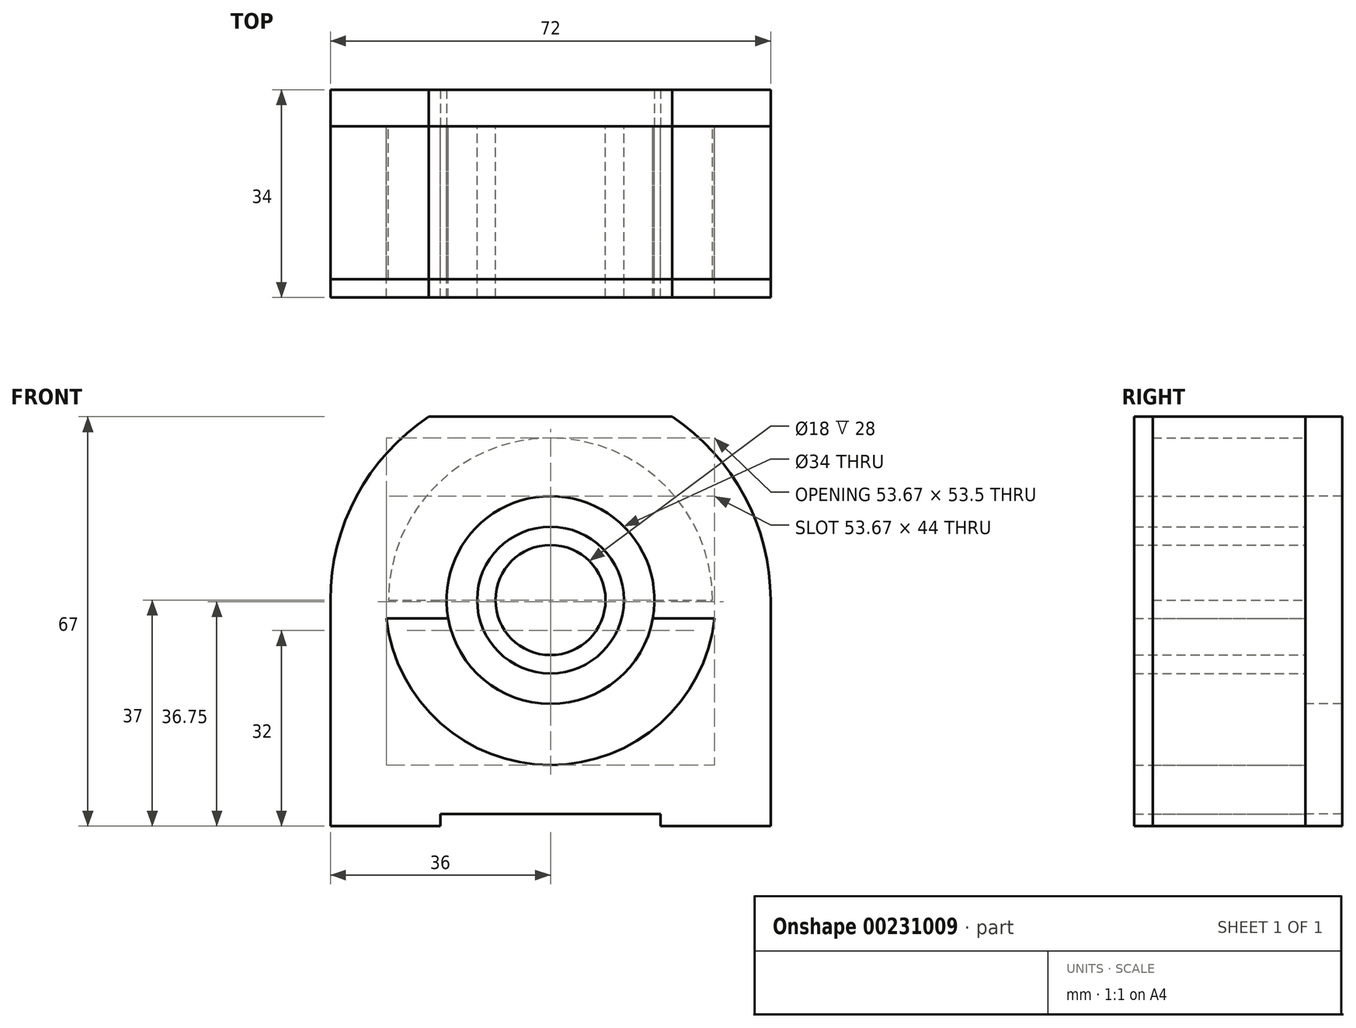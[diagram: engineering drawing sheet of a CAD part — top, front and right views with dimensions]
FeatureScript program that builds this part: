
annotation { "Feature Type Name" : "Feature", "Feature Type Description" : "" }
export const myFeature = defineFeature(function(context is Context, id is Id, definition is map)
    precondition{}
    {
        {
            var Q0;
            Q0=qCreatedBy(makeId("Front.planeOp"),FACE);
            var sketch = newSketch(context, id + "F0", { "sketchPlane" : qUnion([Q0])});
            skLineSegment(sketch, "E0", {"start": v(0, 0) * mm, "end": v(18, 0) * mm});
            skLineSegment(sketch, "E1", {"start": v(72, 0) * mm, "end": v(72, 37) * mm});
            skLineSegment(sketch, "E2", {"start": v(55.9, 67) * mm, "end": v(16.1, 67) * mm});
            skLineSegment(sketch, "E3", {"start": v(0, 37) * mm, "end": v(0, 0) * mm});
            skLineSegment(sketch, "E4", {"start": v(72, 37) * mm, "end": v(-6.12, 37) * mm, "construction": true});
            skLineSegment(sketch, "E5", {"start": v(36, 2) * mm, "end": v(36, 89.75) * mm, "construction": true});
            skPoint(sketch, "E5.endSnap0", {"position": v(36, 67) * mm});
            skLineSegment(sketch, "E6", {"start": v(36, 2) * mm, "end": v(36, 37) * mm, "construction": true});
            skArc(sketch, "E7", {"start": v(16.1, 67) * mm, "mid": v(4.28, 54.02) * mm, "end": v(0, 37) * mm});
            skArc(sketch, "E8", {"start": v(9.17, 34) * mm, "mid": v(36, 10) * mm, "end": v(62.83, 34) * mm});
            skArc(sketch, "E9", {"start": v(62.5, 37) * mm, "mid": v(36, 63.5) * mm, "end": v(9.5, 37) * mm});
            skCircle(sketch, "E10", {"center": v(36, 37) * mm, "radius": 12 * mm});
            skCircle(sketch, "E11", {"center": v(36, 37) * mm, "radius": 9 * mm});
            skPoint(sketch, "E12.orphan", {"position": v(0, 67) * mm});
            skPoint(sketch, "E13.orphan", {"position": v(72, 67) * mm});
            skLineSegment(sketch, "E14.top", {"start": v(18, 2) * mm, "end": v(54, 2) * mm});
            skLineSegment(sketch, "E14.left", {"start": v(18, 0) * mm, "end": v(18, 2) * mm});
            skLineSegment(sketch, "E14.right", {"start": v(54, 0) * mm, "end": v(54, 2) * mm});
            skLineSegment(sketch, "E15.trimOffspring", {"start": v(54, 0) * mm, "end": v(72, 0) * mm});
            skPoint(sketch, "E16.end.orphan", {"position": v(54, 0) * mm});
            skArc(sketch, "E17.trimOffspring", {"start": v(72, 37) * mm, "mid": v(67.72, 54.02) * mm, "end": v(55.9, 67) * mm});
            skPoint(sketch, "E18.orphan", {"position": v(36, 0) * mm});
            skLineSegment(sketch, "E19", {"start": v(0, 0) * mm, "end": v(0, 34) * mm});
            skLineSegment(sketch, "E20", {"start": v(0, 34) * mm, "end": v(72, 34) * mm, "construction": true});
            skLineSegment(sketch, "E21", {"start": v(0, 34) * mm, "end": v(19.27, 34) * mm});
            skLineSegment(sketch, "E22", {"start": v(52.73, 34) * mm, "end": v(72, 34) * mm});
            skLineSegment(sketch, "E23", {"start": v(72, 34) * mm, "end": v(62.83, 34) * mm});
            skLineSegment(sketch, "E24", {"start": v(0, 34) * mm, "end": v(9.17, 34) * mm});
            skLineSegment(sketch, "E25", {"start": v(9.17, 34) * mm, "end": v(9.67, 34) * mm});
            skLineSegment(sketch, "E26", {"start": v(9.67, 34) * mm, "end": v(16.23, 34) * mm});
            skArc(sketch, "E27.trimOffspring", {"start": v(19.27, 34) * mm, "mid": v(36, 20) * mm, "end": v(52.73, 34) * mm});
            skLineSegment(sketch, "E28", {"start": v(9.5, 37) * mm, "end": v(24, 37) * mm});
            skLineSegment(sketch, "E29", {"start": v(48, 37) * mm, "end": v(62.5, 37) * mm});
            skCircle(sketch, "E30", {"center": v(36, 37) * mm, "radius": 17 * mm});
            skSolve(sketch);
        }
        {
            var Q0;
            Q0=makeQuery(id+"F0.imprint","IMPRINT",FACE,{"disambiguationData":[TD([[makeQuery(id+"F0.imprint","IMPRINT",EDGE,{"derivedFrom":sQuery(id+"F0.wireOp",EDGE,"E2")}),1.0]])]});
            var Q1;
            Q1=makeQuery(id+"F0.imprint","IMPRINT",FACE,{"disambiguationData":[TD([[makeQuery(id+"F0.imprint","IMPRINT",EDGE,{"derivedFrom":sQuery(id+"F0.wireOp",EDGE,"E9")}),1.0]])]});
            var Q2;
            Q2=makeQuery(id+"F0.imprint","IMPRINT",FACE,{"disambiguationData":[TD([[makeQuery(id+"F0.imprint","IMPRINT",EDGE,{"derivedFrom":sQuery(id+"F0.wireOp",EDGE,"5V4Lcwkb-Qro4-QzEg-NCux-rp4FajvB0DfL")}),1.0]])]});
            var Q3;
            Q3=makeQuery(id+"F0.imprint","IMPRINT",FACE,{"disambiguationData":[TD([[makeQuery(id+"F0.imprint","IMPRINT",EDGE,{"derivedFrom":sQuery(id+"F0.wireOp",EDGE,"t3pJTo9W-rxlE-v0ZQ-Fyb9-gExOxGsqtmdi")}),1.0]])]});
            var Q4;
            Q4=makeQuery(id+"F0.imprint","IMPRINT",FACE,{"disambiguationData":[TD([[makeQuery(id+"F0.imprint","IMPRINT",EDGE,{"derivedFrom":sQuery(id+"F0.wireOp",EDGE,"E10")}),1.0]])]});
            var Q5;
            Q5=makeQuery(id+"F0.imprint","IMPRINT",FACE,{"disambiguationData":[TD([[makeQuery(id+"F0.imprint","IMPRINT",EDGE,{"derivedFrom":sQuery(id+"F0.wireOp",EDGE,"E0")}),1.0]])]});
            extrude(context, id + "F1", {"entities" : qUnion([Q0, Q1, Q2, Q3, Q4, Q5]), "depth" : 28 * mm});
        }
        {
            var Q0;
            Q0=makeQuery(id+"F0.imprint","IMPRINT",FACE,{"disambiguationData":[TD([[makeQuery(id+"F0.imprint","IMPRINT",EDGE,{"derivedFrom":sQuery(id+"F0.wireOp",EDGE,"t3pJTo9W-rxlE-v0ZQ-Fyb9-gExOxGsqtmdi")}),1.0]])]});
            var Q1;
            Q1=makeQuery(id+"F0.imprint","IMPRINT",FACE,{"disambiguationData":[TD([[makeQuery(id+"F0.imprint","IMPRINT",EDGE,{"derivedFrom":sQuery(id+"F0.wireOp",EDGE,"5V4Lcwkb-Qro4-QzEg-NCux-rp4FajvB0DfL")}),1.0]])]});
            var Q2;
            Q2=makeQuery(id+"F0.imprint","IMPRINT",FACE,{"disambiguationData":[TD([[makeQuery(id+"F0.imprint","IMPRINT",EDGE,{"derivedFrom":sQuery(id+"F0.wireOp",EDGE,"E9")}),1.0]])]});
            var Q3;
            Q3=makeQuery(id+"F0.imprint","IMPRINT",FACE,{"disambiguationData":[TD([[makeQuery(id+"F0.imprint","IMPRINT",EDGE,{"derivedFrom":sQuery(id+"F0.wireOp",EDGE,"E2")}),1.0]])]});
            var Q4;
            Q4=makeQuery(id+"F0.imprint","IMPRINT",FACE,{"disambiguationData":[TD([[makeQuery(id+"F0.imprint","IMPRINT",EDGE,{"derivedFrom":sQuery(id+"F0.wireOp",EDGE,"E0")}),1.0]])]});
            var Q5;
            Q5=makeQuery(id+"F0.imprint","IMPRINT",FACE,{"disambiguationData":[TD([[makeQuery(id+"F0.imprint","IMPRINT",EDGE,{"derivedFrom":sQuery(id+"F0.wireOp",EDGE,"E8")}),1.0]])]});
            extrude(context, id + "F2", {"entities" : qUnion([Q0, Q1, Q2, Q3, Q4, Q5]), "oppositeDirection" : true, "depth" : 6 * mm});
        }
        {
            var Q0;
            Q0 = qSketchRegion(id + "F0", true);
            extrude(context, id + "F3", {"entities" : qUnion([Q0]), "depth" : 25 * mm});
        }
    });
